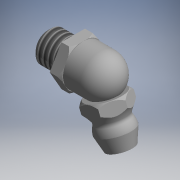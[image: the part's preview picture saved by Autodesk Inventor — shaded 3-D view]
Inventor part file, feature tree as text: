
AUTODESK INVENTOR PART (.ipt)
format: ipt  version: 2022 (Build 260153000, 153)  size: 220,672 bytes
history: native  units: mm (DEFAULTED — no unit token found)
features: other x7, sketch x5, revolve x3, extrude x2, thread x1
ambient origin geometry x8: Origin, YZ Plane, XZ Plane, XY Plane, X Axis, Y Axis, Z Axis, Center Point
bodies: Solid1 (feature_tree)
feature tree (18):
  revolve  "Revolution1"  [1 undecoded]
  thread  "Thread1"  [1 undecoded]
  revolve  "Revolution2"  Angle=360.0deg
  extrude  "Extrusion1"  TaperAngle=0.0deg  [1 undecoded]
  revolve  "Revolution3"  [1 undecoded]
  extrude  "Extrusion2"  [1 undecoded]
  other  "n_j_XY"
  other  "n_j_YZ"
  other  "n_j_ZX"
  other  "n_j_X"
  other  "n_j_Y"
  other  "n_j_Z"
  other  "n_j_Center"
  sketch  "Sketch_1"  dims[d0=360.0deg d1=3.84338mm d2=0.0mm d3=360.0deg]
  sketch  "Sketch_5"  dims[d4=5.0mm d5=0.0mm d6=360.0deg]
  sketch  "Sketch_13"  dims[d7=2.5mm d8=0.0mm d9=0.0mm]
  sketch  "Sketch_17"
  sketch  "Sketch_18"
note: 5 required parameter values undecoded (feature->parameter linkage not recoverable at this tier; creation-order binding heuristic only, values carry confidence <= 0.55)